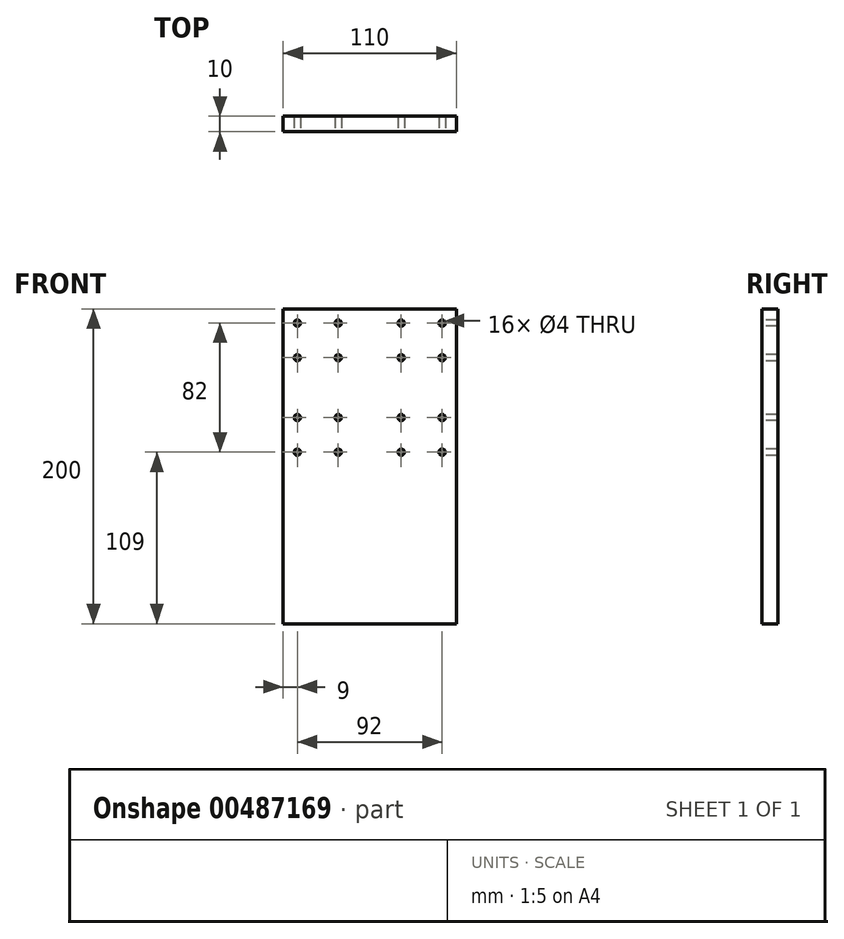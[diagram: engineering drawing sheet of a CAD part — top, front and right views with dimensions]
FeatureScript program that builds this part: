
annotation { "Feature Type Name" : "Feature", "Feature Type Description" : "" }
export const myFeature = defineFeature(function(context is Context, id is Id, definition is map)
    precondition{}
    {
        {
            var Q0;
            Q0=qCreatedBy(makeId("Front.planeOp"),FACE);
            var sketch = newSketch(context, id + "F0", { "sketchPlane" : qUnion([Q0])});
            skLineSegment(sketch, "E0.bottom", {"start": v(-55, 50) * mm, "end": v(55, 50) * mm});
            skLineSegment(sketch, "E0.top", {"start": v(-55, -50) * mm, "end": v(55, -50) * mm});
            skLineSegment(sketch, "E0.left", {"start": v(-55, 50) * mm, "end": v(-55, -50) * mm});
            skLineSegment(sketch, "E0.right", {"start": v(55, 50) * mm, "end": v(55, -50) * mm});
            skSolve(sketch);
        }
        {
            var Q0;
            Q0 = qSketchRegion(id + "F0", true);
            extrude(context, id + "F1", {"entities" : qUnion([Q0]), "depth" : 10 * mm});
        }
        {
            var Q0;
            Q0=makeQuery(id+"F1.opExtrude","CAP_FACE",FACE,{"disambiguationData":[OSD([sQuery(id+"F0.wireOp",EDGE,"E0.bottom"),sQuery(id+"F0.wireOp",EDGE,"E0.top"),sQuery(id+"F0.wireOp",EDGE,"E0.left"),sQuery(id+"F0.wireOp",EDGE,"E0.right")])],"isStart":false});
            var sketch = newSketch(context, id + "F2", { "sketchPlane" : qUnion([Q0])});
            skCircle(sketch, "E1", {"center": v(-46, 41) * mm, "radius": 2 * mm});
            skCircle(sketch, "E2", {"center": v(-20, 41) * mm, "radius": 2 * mm});
            skCircle(sketch, "E3", {"center": v(-46, 19) * mm, "radius": 2 * mm});
            skCircle(sketch, "E4", {"center": v(-20, 19) * mm, "radius": 2 * mm});
            skCircle(sketch, "E5.MirrorC", {"center": v(46, 41) * mm, "radius": 2 * mm});
            skCircle(sketch, "E6.MirrorC", {"center": v(20, 41) * mm, "radius": 2 * mm});
            skCircle(sketch, "E7.MirrorC", {"center": v(20, 19) * mm, "radius": 2 * mm});
            skCircle(sketch, "E8.MirrorC", {"center": v(46, 19) * mm, "radius": 2 * mm});
            skCircle(sketch, "E9.MirrorC", {"center": v(-46, -19) * mm, "radius": 2 * mm});
            skCircle(sketch, "E10.MirrorC", {"center": v(-46, -41) * mm, "radius": 2 * mm});
            skCircle(sketch, "E11.MirrorC", {"center": v(-20, -19) * mm, "radius": 2 * mm});
            skCircle(sketch, "E12.MirrorC", {"center": v(-20, -41) * mm, "radius": 2 * mm});
            skCircle(sketch, "E13.MirrorC", {"center": v(20, -41) * mm, "radius": 2 * mm});
            skCircle(sketch, "E14.MirrorC", {"center": v(46, -41) * mm, "radius": 2 * mm});
            skCircle(sketch, "E15.MirrorC", {"center": v(46, -19) * mm, "radius": 2 * mm});
            skCircle(sketch, "E16.MirrorC", {"center": v(20, -19) * mm, "radius": 2 * mm});
            skSolve(sketch);
        }
        {
            var Q0;
            Q0 = qSketchRegion(id + "F2", true);
            extrude(context, id + "F3", {"entities" : qUnion([Q0]), "operationType" : NewBodyOperationType.REMOVE, "oppositeDirection" : true, "depth" : 25 * mm});
        }
        {
            var Q0;
            Q0=qCreatedBy(makeId("Front.planeOp"),FACE);
            var sketch = newSketch(context, id + "F4", { "sketchPlane" : qUnion([Q0])});
            skLineSegment(sketch, "E17.bottom", {"start": v(-55, -50) * mm, "end": v(55, -50) * mm});
            skLineSegment(sketch, "E17.top", {"start": v(-55, -150) * mm, "end": v(55, -150) * mm});
            skLineSegment(sketch, "E17.left", {"start": v(-55, -50) * mm, "end": v(-55, -150) * mm});
            skLineSegment(sketch, "E17.right", {"start": v(55, -50) * mm, "end": v(55, -150) * mm});
            skSolve(sketch);
        }
        {
            var Q0;
            Q0 = qSketchRegion(id + "F4", true);
            extrude(context, id + "F5", {"entities" : qUnion([Q0]), "operationType" : NewBodyOperationType.ADD, "depth" : 10 * mm});
        }
    });
